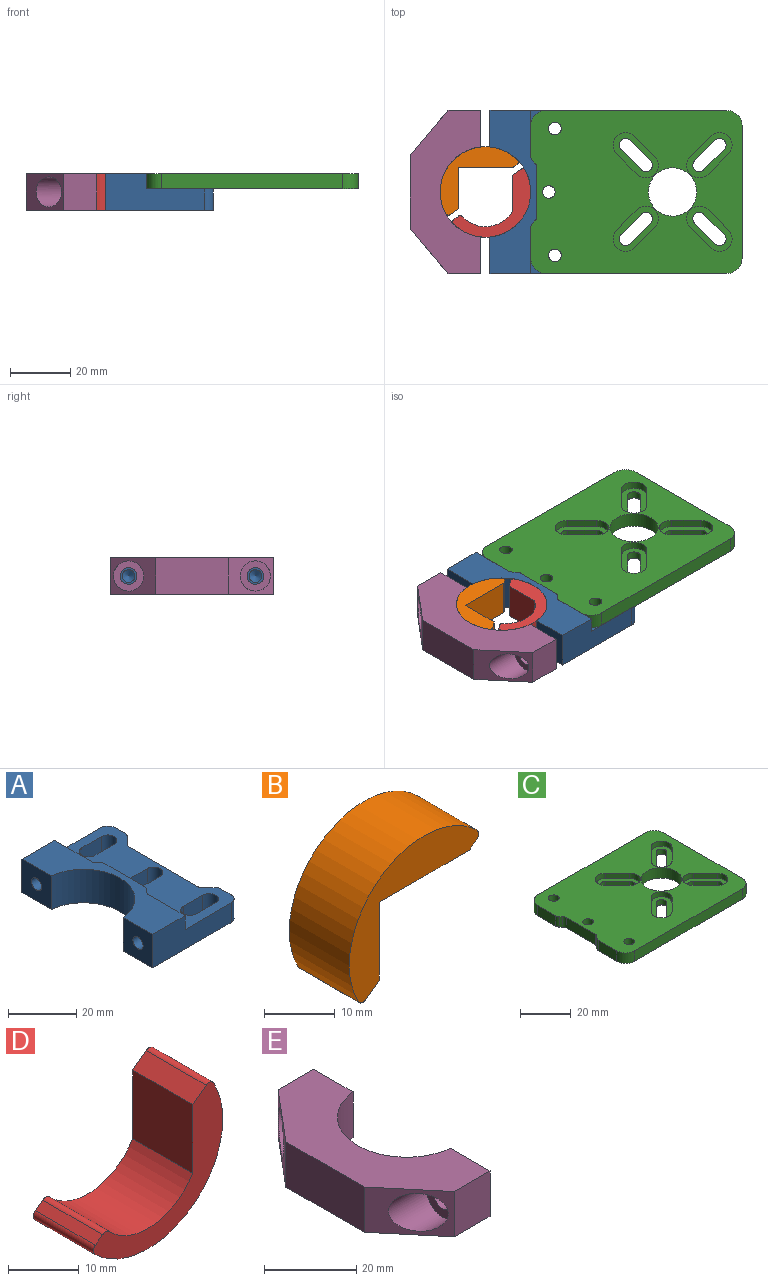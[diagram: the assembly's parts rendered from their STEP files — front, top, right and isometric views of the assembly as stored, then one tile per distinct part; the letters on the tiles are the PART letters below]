
ASSEMBLY  parts=5 mates=7
PART A: 44 faces, bbox 35.5x54x12 mm
  f0: plane 7x4.17mm, normal (1,0,0), area 29.2mm2, adj f16,f20,f25,f34
  f1: plane 28.34x7mm, normal (1,0,0), area 198.4mm2, adj f21,f22,f25,f34
  f2: plane 7x4.17mm, normal (1,0,0), area 29.2mm2, adj f15,f19,f25,f34
  f3: cylinder r=2.7mm len=7mm, axis (0,0,1), area 59.4mm2, adj f4,f6,f25,f34
  f4: plane 8x7mm, normal (0,-1,0), area 56mm2, adj f3,f5,f25,f34
  f5: cylinder r=2.7mm len=7mm, axis (0,0,1), area 59.4mm2, adj f4,f6,f25,f34
  f6: plane 8x7mm, normal (0,1,0), area 56mm2, adj f3,f5,f25,f34
  f7: cylinder r=2.7mm len=7mm, axis (0,0,1), area 59.4mm2, adj f8,f10,f25,f34
  f8: plane 8x7mm, normal (0,-1,0), area 56mm2, adj f7,f9,f25,f34
  f9: cylinder r=2.7mm len=7mm, axis (0,0,1), area 59.4mm2, adj f8,f10,f25,f34
  f10: plane 8x7mm, normal (0,1,0), area 56mm2, adj f7,f9,f25,f34
  f11: cylinder r=2.7mm len=7mm, axis (0,0,1), area 59.4mm2, adj f12,f14,f25,f34
  f12: plane 8x7mm, normal (0,-1,0), area 56mm2, adj f11,f13,f25,f34
  f13: cylinder r=2.7mm len=7mm, axis (0,0,1), area 59.4mm2, adj f12,f14,f25,f34
  f14: plane 8x7mm, normal (0,1,0), area 56mm2, adj f11,f13,f25,f34
  f15: cylinder r=3mm len=7mm, axis (0,0,1), area 33mm2, adj f2,f24,f25,f34
  f16: cylinder r=3mm len=7mm, axis (0,0,1), area 33mm2, adj f0,f23,f25,f34
  f17: plane 7x2.83mm, normal (0.71,-0.71,0), area 28mm2, adj f20,f22,f25,f34
  f18: plane 7x2.83mm, normal (0.71,0.71,0), area 28mm2, adj f19,f21,f25,f34
  f19: cylinder r=2mm len=7mm, axis (0,0,-1), area 11mm2, adj f2,f18,f25,f34
  f20: cylinder r=2mm len=7mm, axis (0,0,1), area 11mm2, adj f0,f17,f25,f34
  f21: cylinder r=2mm len=7mm, axis (0,0,1), area 11mm2, adj f1,f18,f25,f34
  f22: cylinder r=2mm len=7mm, axis (0,0,1), area 11mm2, adj f1,f17,f25,f34
  f23: plane 32.5x12mm, normal (0,1,0), area 295mm2, adj f16,f25,f26,f29,f34,f35
  f24: plane 32.5x12mm, normal (0,-1,0), area 295mm2, adj f15,f25,f26,f28,f34,f36
  f25: plane 54x35.5mm, normal (0,0,-1), area 1270.3mm2, adj f0,f1,f2,f3,f4,f5,f6,f7
  f26: plane 54x15.5mm, normal (0,0,1), area 460.5mm2, adj f23,f24,f27,f28,f29,f35,f36,f37
  f27: cylinder r=15mm len=29.85mm, axis (0,0,1), area 529.4mm2, adj f25,f26,f28,f29
  f28: plane 12.08x12mm, normal (-1,0,0), area 131mm2, adj f24,f25,f26,f27,f31
  f29: plane 12.08x12mm, normal (-1,0,0), area 131mm2, adj f23,f25,f26,f27,f33
  f30: cone r=2.1mm half-angle=59deg, axis (-1,0,0), area 16.2mm2, adj f31
  f31: cylinder r=2.1mm len=11mm, axis (-1,0,0), area 145.1mm2, adj f28,f30
  f32: cone r=2.1mm half-angle=59deg, axis (-1,0,0), area 16.2mm2, adj f33
  f33: cylinder r=2.1mm len=11mm, axis (-1,0,0), area 145.1mm2, adj f29,f32
  f34: plane 54x22mm, normal (0,0,1), area 809.8mm2, adj f0,f1,f2,f3,f4,f5,f6,f7
  f35: plane 15.17x5mm, normal (1,0,0), area 75.9mm2, adj f23,f26,f34,f43
  f36: plane 15.17x5mm, normal (1,0,0), area 75.9mm2, adj f24,f26,f34,f40
  f37: plane 5x0.83mm, normal (0.71,-0.71,0), area 5.9mm2, adj f26,f34,f40,f41
  f38: plane 16.34x5mm, normal (1,0,0), area 81.7mm2, adj f26,f34,f41,f42
  f39: plane 5x0.83mm, normal (0.71,0.71,0), area 5.9mm2, adj f26,f34,f42,f43
  f40: cylinder r=2mm len=5mm, axis (0,0,-1), area 7.9mm2, adj f26,f34,f36,f37
  f41: cylinder r=2mm len=5mm, axis (0,0,1), area 7.9mm2, adj f26,f34,f37,f38
  f42: cylinder r=2mm len=5mm, axis (0,0,1), area 7.9mm2, adj f26,f34,f38,f39
  f43: cylinder r=2mm len=5mm, axis (0,0,-1), area 7.9mm2, adj f26,f34,f35,f39
PART B: 9 faces, bbox 25.9x12x22.7 mm
  f0: plane 13.5x12mm, normal (1,0,0), area 162mm2, adj f1,f4,f5,f6
  f1: plane 12x2.69mm, normal (0.6,0,-0.8), area 40.3mm2, adj f0,f5,f6,f8
  f2: cylinder r=15mm len=25.59mm, axis (0,-1,0), area 513.9mm2, adj f5,f6,f7,f8
  f3: plane 12x1.49mm, normal (0.6,0,-0.8), area 22.3mm2, adj f4,f5,f6,f7
  f4: plane 18x12mm, normal (0,0,-1), area 216mm2, adj f0,f3,f5,f6
  f5: plane 25.89x22.71mm, normal (0,1,0), area 201.4mm2, adj f0,f1,f2,f3,f4,f7,f8
  f6: plane 25.89x22.71mm, normal (0,-1,0), area 201.4mm2, adj f0,f1,f2,f3,f4,f7,f8
  f7: cylinder r=1mm len=12mm, axis (0,-1,0), area 20.6mm2, adj f2,f3,f5,f6
  f8: cylinder r=1mm len=12mm, axis (0,-1,0), area 20.6mm2, adj f1,f2,f5,f6
PART C: 58 faces, bbox 70x54x5 mm
  f0: plane 70x54mm, normal (0,0,1), area 2944.1mm2, adj f2,f19,f20,f21,f22,f23,f24,f25
  f1: plane 70x54mm, normal (0,0,-1), area 3254.4mm2, adj f2,f3,f4,f5,f6,f7,f8,f9
  f2: plane 10.17x5mm, normal (-1,0,0), area 50.9mm2, adj f0,f1,f30,f57
  f3: cylinder r=2.15mm len=3.67mm, axis (0,0,-1), area 16.9mm2, adj f1,f4,f6,f50
  f4: plane 6.72x6.72mm, normal (0.71,0.71,0), area 23.8mm2, adj f1,f3,f5,f50
  f5: cylinder r=2.15mm len=3.67mm, axis (0,0,-1), area 16.9mm2, adj f1,f4,f6,f50
  f6: plane 6.72x6.72mm, normal (-0.71,-0.71,0), area 23.8mm2, adj f1,f3,f5,f50
  f7: cylinder r=2.15mm len=3.67mm, axis (0,0,-1), area 16.9mm2, adj f1,f8,f10,f45
  f8: plane 6.72x6.72mm, normal (-0.71,0.71,0), area 23.8mm2, adj f1,f7,f9,f45
  f9: cylinder r=2.15mm len=3.67mm, axis (0,0,-1), area 16.9mm2, adj f1,f8,f10,f45
  f10: plane 6.72x6.72mm, normal (0.71,-0.71,0), area 23.8mm2, adj f1,f7,f9,f45
  f11: cylinder r=2.15mm len=3.67mm, axis (0,0,-1), area 16.9mm2, adj f1,f12,f14,f40
  f12: plane 6.72x6.72mm, normal (-0.71,-0.71,0), area 23.8mm2, adj f1,f11,f13,f40
  f13: cylinder r=2.15mm len=3.67mm, axis (0,0,-1), area 16.9mm2, adj f1,f12,f14,f40
  f14: plane 6.72x6.72mm, normal (0.71,0.71,0), area 23.8mm2, adj f1,f11,f13,f40
  f15: cylinder r=2.15mm len=3.67mm, axis (0,0,-1), area 16.9mm2, adj f1,f16,f18,f35
  f16: plane 6.72x6.72mm, normal (0.71,-0.71,0), area 23.8mm2, adj f1,f15,f17,f35
  f17: cylinder r=2.15mm len=3.67mm, axis (0,0,-1), area 16.9mm2, adj f1,f16,f18,f35
  f18: plane 6.72x6.72mm, normal (-0.71,0.71,0), area 23.8mm2, adj f1,f15,f17,f35
  f19: plane 10.17x5mm, normal (-1,0,0), area 50.9mm2, adj f0,f1,f29,f56
  f20: plane 60x5mm, normal (0,-1,0), area 300mm2, adj f0,f1,f27,f29
  f21: plane 44x5mm, normal (1,0,0), area 220mm2, adj f0,f1,f27,f28
  f22: plane 60x5mm, normal (0,1,0), area 300mm2, adj f0,f1,f28,f30
  f23: cylinder r=8mm len=16mm, axis (0,0,-1), area 251.3mm2, adj f0,f1
  f24: cylinder r=2.1mm len=5mm, axis (0,0,1), area 66mm2, adj f0,f1
  f25: cylinder r=2.1mm len=5mm, axis (0,0,1), area 66mm2, adj f0,f1
  f26: cylinder r=2.1mm len=5mm, axis (0,0,1), area 66mm2, adj f0,f1
  f27: cylinder r=5mm len=5mm, axis (0,0,-1), area 39.3mm2, adj f0,f1,f20,f21
  f28: cylinder r=5mm len=5mm, axis (0,0,-1), area 39.3mm2, adj f0,f1,f21,f22
  f29: cylinder r=5mm len=5mm, axis (0,0,-1), area 39.3mm2, adj f0,f1,f19,f20
  f30: cylinder r=5mm len=5mm, axis (0,0,-1), area 39.3mm2, adj f0,f1,f2,f22
  f31: cylinder r=4.15mm len=7.08mm, axis (0,0,1), area 32.6mm2, adj f0,f32,f34,f35
  f32: plane 6.72x6.72mm, normal (0.71,-0.71,0), area 23.7mm2, adj f0,f31,f33,f35
  f33: cylinder r=4.15mm len=7.08mm, axis (0,0,1), area 32.6mm2, adj f0,f32,f34,f35
  f34: plane 6.72x6.72mm, normal (-0.71,0.71,0), area 23.7mm2, adj f0,f31,f33,f35
  f35: plane 15.02x15.02mm, normal (0,0,1), area 77.6mm2, adj f15,f16,f17,f18,f31,f32,f33,f34
  f36: cylinder r=4.15mm len=7.08mm, axis (0,0,1), area 32.6mm2, adj f0,f37,f39,f40
  f37: plane 6.72x6.72mm, normal (-0.71,-0.71,0), area 23.7mm2, adj f0,f36,f38,f40
  f38: cylinder r=4.15mm len=7.08mm, axis (0,0,1), area 32.6mm2, adj f0,f37,f39,f40
  f39: plane 6.72x6.72mm, normal (0.71,0.71,0), area 23.7mm2, adj f0,f36,f38,f40
  f40: plane 15.02x15.02mm, normal (0,0,1), area 77.6mm2, adj f11,f12,f13,f14,f36,f37,f38,f39
  f41: cylinder r=4.15mm len=7.08mm, axis (0,0,1), area 32.6mm2, adj f0,f42,f44,f45
  f42: plane 6.72x6.72mm, normal (-0.71,0.71,0), area 23.7mm2, adj f0,f41,f43,f45
  f43: cylinder r=4.15mm len=7.08mm, axis (0,0,1), area 32.6mm2, adj f0,f42,f44,f45
  f44: plane 6.72x6.72mm, normal (0.71,-0.71,0), area 23.7mm2, adj f0,f41,f43,f45
  f45: plane 15.02x15.02mm, normal (0,0,1), area 77.6mm2, adj f7,f8,f9,f10,f41,f42,f43,f44
  f46: cylinder r=4.15mm len=7.08mm, axis (0,0,1), area 32.6mm2, adj f0,f47,f49,f50
  f47: plane 6.72x6.72mm, normal (0.71,0.71,0), area 23.7mm2, adj f0,f46,f48,f50
  f48: cylinder r=4.15mm len=7.08mm, axis (0,0,1), area 32.6mm2, adj f0,f47,f49,f50
  f49: plane 6.72x6.72mm, normal (-0.71,-0.71,0), area 23.7mm2, adj f0,f46,f48,f50
  f50: plane 15.02x15.02mm, normal (0,0,1), area 77.6mm2, adj f3,f4,f5,f6,f46,f47,f48,f49
  f51: plane 16.34x5mm, normal (-1,0,0), area 81.7mm2, adj f0,f1,f54,f55
  f52: plane 5x0.83mm, normal (-0.71,0.71,0), area 5.9mm2, adj f0,f1,f55,f56
  f53: plane 5x0.83mm, normal (-0.71,-0.71,0), area 5.9mm2, adj f0,f1,f54,f57
  f54: cylinder r=2mm len=5mm, axis (0,0,-1), area 7.9mm2, adj f0,f1,f51,f53
  f55: cylinder r=2mm len=5mm, axis (0,0,1), area 7.9mm2, adj f0,f1,f51,f52
  f56: cylinder r=2mm len=5mm, axis (0,0,-1), area 7.9mm2, adj f0,f1,f19,f52
  f57: cylinder r=2mm len=5mm, axis (0,0,-1), area 7.9mm2, adj f0,f1,f2,f53
PART D: 10 faces, bbox 25.9x12x22.7 mm
  f0: plane 12x2.69mm, normal (-0.6,0,0.8), area 40.3mm2, adj f4,f5,f6,f9
  f1: cylinder r=15mm len=25.59mm, axis (0,-1,0), area 513.9mm2, adj f5,f6,f7,f9
  f2: plane 12x1.46mm, normal (-0.6,0,0.8), area 21.8mm2, adj f5,f6,f7,f8
  f3: cylinder r=10.5mm len=16.7mm, axis (0,-1,0), area 233.4mm2, adj f4,f5,f6,f8
  f4: plane 12x11.91mm, normal (-1,0,0), area 142.9mm2, adj f0,f3,f5,f6
  f5: plane 25.89x22.71mm, normal (0,1,0), area 164.5mm2, adj f0,f1,f2,f3,f4,f7,f8,f9
  f6: plane 25.89x22.71mm, normal (0,-1,0), area 164.5mm2, adj f0,f1,f2,f3,f4,f7,f8,f9
  f7: cylinder r=1mm len=12mm, axis (0,-1,0), area 20.6mm2, adj f1,f2,f5,f6
  f8: cylinder r=1mm len=12mm, axis (0,-1,0), area 17.6mm2, adj f2,f3,f5,f6
  f9: cylinder r=1mm len=12mm, axis (0,-1,0), area 20.6mm2, adj f0,f1,f5,f6
PART E: 16 faces, bbox 25.3x55.8x13.8 mm
  f0: plane 16.76x14.35mm, normal (-0.77,-0.64,0), area 132.4mm2, adj f1,f4,f5,f6,f15
  f1: plane 24x12mm, normal (-1,0,0), area 288mm2, adj f0,f2,f4,f5
  f2: plane 16.76x14.35mm, normal (-0.77,0.64,0), area 132.4mm2, adj f1,f4,f5,f7,f12
  f3: cylinder r=15mm len=29.85mm, axis (0,0,1), area 529.4mm2, adj f4,f5,f8,f9
  f4: plane 54x23.5mm, normal (0,0,1), area 771.7mm2, adj f0,f1,f2,f3,f6,f7,f8,f9
  f5: plane 54x23.5mm, normal (0,0,-1), area 771.7mm2, adj f0,f1,f2,f3,f6,f7,f8,f9
  f6: plane 12x10.91mm, normal (0,-1,0), area 131mm2, adj f0,f4,f5,f9
  f7: plane 12x10.91mm, normal (0,1,0), area 131mm2, adj f2,f4,f5,f8
  f8: plane 12.08x12mm, normal (1,0,0), area 121.1mm2, adj f3,f4,f5,f7,f10
  f9: plane 12.08x12mm, normal (1,0,0), area 121.1mm2, adj f3,f4,f5,f6,f13
  f10: cylinder r=2.75mm len=8.5mm, axis (-1,0,0), area 146.9mm2, adj f8,f11
  f11: plane 10x10mm, normal (-1,0,0), area 54.8mm2, adj f10,f12
  f12: cylinder r=5mm len=11.64mm, axis (-1,0,0), area 229.5mm2, adj f2,f11
  f13: cylinder r=2.75mm len=8.5mm, axis (-1,0,0), area 146.9mm2, adj f9,f14
  f14: plane 10x10mm, normal (-1,0,0), area 54.8mm2, adj f13,f15
  f15: cylinder r=5mm len=11.64mm, axis (-1,0,0), area 229.5mm2, adj f0,f14
PLACE A t=(0,0,-4.78)mm fixed
PLACE B rot(axis=(-1,0,0),90deg) t=(25,26,-4.78)mm
PLACE C t=(40,0,-9.78)mm
PLACE D rot(axis=(-1,0,0),90deg) t=(25,26,-4.78)mm
PLACE E t=(0,0,-4.78)mm
MATE fastened C.f25 <-> A.f11  axis (0,0,-1) through (46,27,-9.78)mm
MATE cylindrical E.f3 <-> B.f2  axis (0,0,1) through (25,27,-4.78)mm
MATE cylindrical E.f10 <-> A.f32  axis (1,0,0) through (23.5,48,-10.78)mm
MATE cylindrical B.f2 <-> A.f27  axis (0,0,1) through (25,27,-4.78)mm
MATE cylindrical A.f30 <-> E.f13  axis (-1,0,0) through (26.5,6,-10.78)mm
MATE cylindrical A.f27 <-> D.f1  axis (0,0,1) through (25,27,-4.78)mm
MATE planar C.f1 <-> A.f34  axis (0,0,-1) through (74.21,27,-9.78)mm
